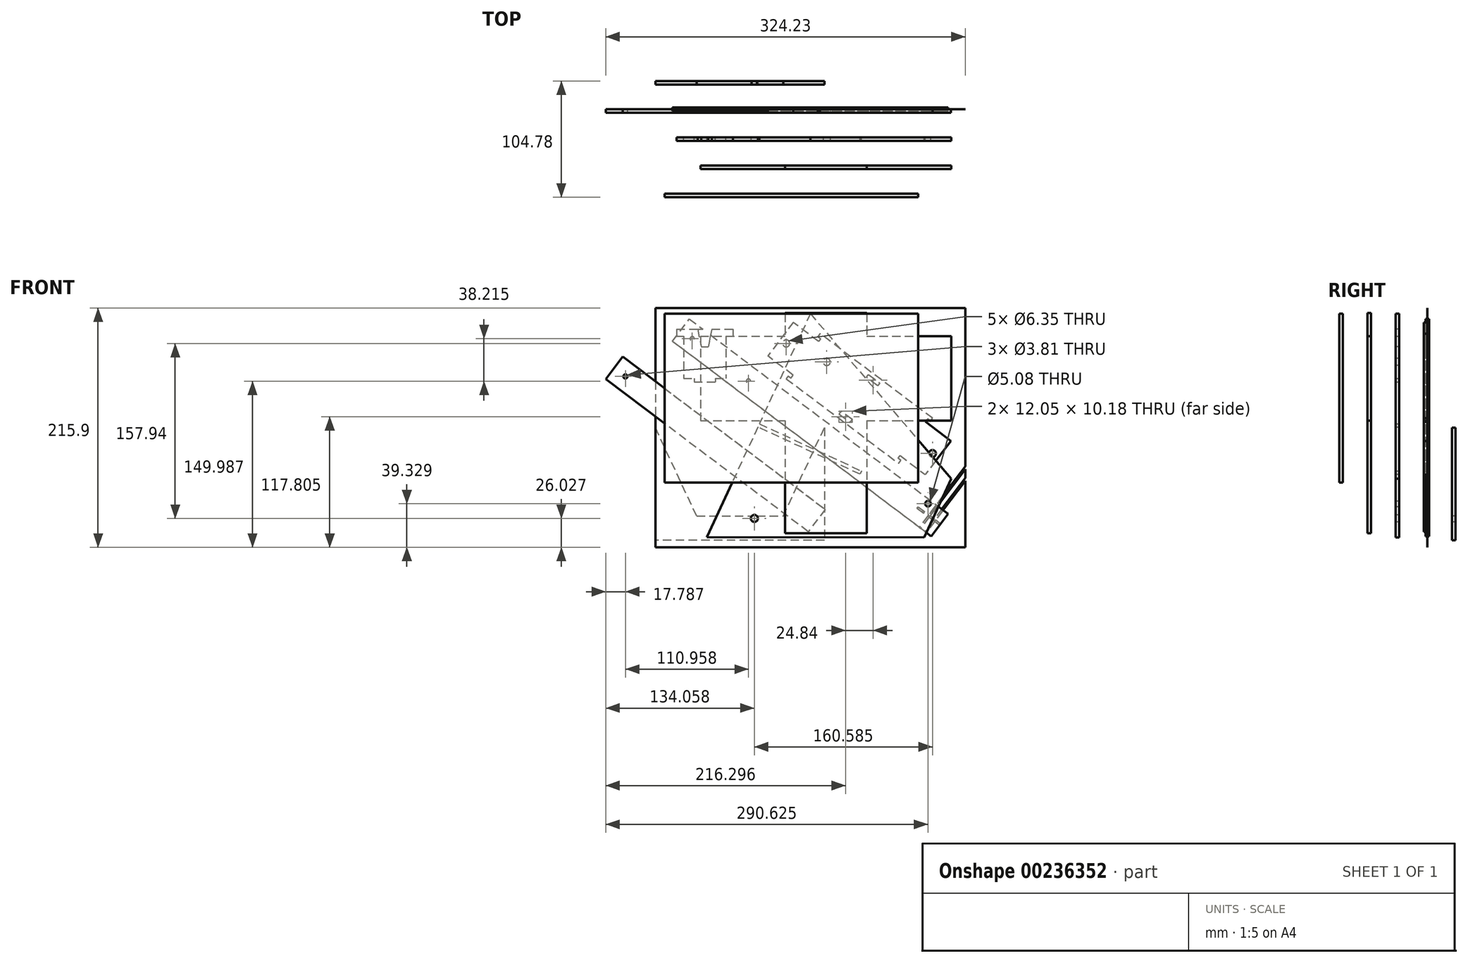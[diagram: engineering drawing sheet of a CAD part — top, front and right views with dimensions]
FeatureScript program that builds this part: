
annotation { "Feature Type Name" : "Feature", "Feature Type Description" : "" }
export const myFeature = defineFeature(function(context is Context, id is Id, definition is map)
    precondition{}
    {
        {
            var Q0;
            Q0=qCreatedBy(makeId("Front.planeOp"),FACE);
            var sketch = newSketch(context, id + "F0", { "sketchPlane" : qUnion([Q0])});
            skLineSegment(sketch, "E0.bottom", {"start": v(139.7, 107.95) * mm, "end": v(-139.7, 107.95) * mm});
            skLineSegment(sketch, "E0.top", {"start": v(139.7, -107.95) * mm, "end": v(-139.7, -107.95) * mm});
            skLineSegment(sketch, "E0.left", {"start": v(139.7, 107.95) * mm, "end": v(139.7, -107.95) * mm});
            skLineSegment(sketch, "E0.right", {"start": v(-139.7, 107.95) * mm, "end": v(-139.7, -107.95) * mm});
            skPoint(sketch, "E0.middle", {"position": v(0, 0) * mm});
            skSolve(sketch);
        }
        {
            var Q0;
            Q0=qCreatedBy(makeId("Front.planeOp"),FACE);
            var sketch = newSketch(context, id + "F1", { "sketchPlane" : qUnion([Q0])});
            skLineSegment(sketch, "E1.bottom", {"start": v(139.7, 107.95) * mm, "end": v(-139.7, 107.95) * mm, "construction": true});
            skLineSegment(sketch, "E1.top", {"start": v(139.7, -107.95) * mm, "end": v(-139.7, -107.95) * mm, "construction": true});
            skLineSegment(sketch, "E1.left", {"start": v(139.7, 107.95) * mm, "end": v(139.7, -107.95) * mm, "construction": true});
            skLineSegment(sketch, "E1.right", {"start": v(-139.7, 107.95) * mm, "end": v(-139.7, -107.95) * mm, "construction": true});
            skPoint(sketch, "E1.middle", {"position": v(0, 0) * mm});
            skLineSegment(sketch, "E2", {"start": v(-109, 98.04) * mm, "end": v(124.28, -77.75) * mm});
            skLineSegment(sketch, "E3", {"start": v(124.28, -77.75) * mm, "end": v(109, -98.04) * mm});
            skLineSegment(sketch, "E4", {"start": v(109, -98.04) * mm, "end": v(-124.28, 77.75) * mm});
            skLineSegment(sketch, "E5", {"start": v(-124.28, 77.75) * mm, "end": v(-109, 98.04) * mm});
            skLineSegment(sketch, "E6", {"start": v(-116.64, 87.9) * mm, "end": v(116.64, -87.9) * mm, "construction": true});
            skCircle(sketch, "E7", {"center": v(-55.78, 42.04) * mm, "radius": 1.9 * mm});
            skCircle(sketch, "E8", {"center": v(-106.5, 80.25) * mm, "radius": 1.9 * mm});
            skSolve(sketch);
        }
        {
            var Q0;
            Q0 = qSketchRegion(id + "F1", true);
            extrude(context, id + "F2", {"entities" : qUnion([Q0]), "endBound" : BoundingType.SYMMETRIC, "depth" : 3.17 * mm});
        }
        {
            var Q0;
            Q0=qCreatedBy(makeId("Front.planeOp"),FACE);
            cPlane(context, id + "F3", {"entities" : qUnion([Q0]), "cplaneType" : CPlaneType.OFFSET, "offset" : 25.4 * mm, "width" : 152.4 * mm, "height" : 152.4 * mm});
        }
        {
            var Q0;
            Q0=qCreatedBy(id+"F3.planeOp",FACE);
            var sketch = newSketch(context, id + "F4", { "sketchPlane" : qUnion([Q0])});
            skLineSegment(sketch, "E9", {"start": v(0, 102.87) * mm, "end": v(127, -46.1) * mm});
            skLineSegment(sketch, "E10", {"start": v(102.48, -99.13) * mm, "end": v(-93.28, -98.86) * mm});
            skLineSegment(sketch, "E11", {"start": v(0, 102.87) * mm, "end": v(-45.97, 3.45) * mm});
            skCircle(sketch, "E12", {"center": v(106.1, -68.62) * mm, "radius": 2.54 * mm});
            skLineSegment(sketch, "E13", {"start": v(-45.97, 3.45) * mm, "end": v(46.24, -39.2) * mm});
            skLineSegment(sketch, "E14", {"start": v(46.24, -39.2) * mm, "end": v(44.91, -42.08) * mm});
            skLineSegment(sketch, "E15", {"start": v(44.91, -42.08) * mm, "end": v(-47.3, 0.57) * mm});
            skLineSegment(sketch, "E16.trimOffspring", {"start": v(-47.3, 0.57) * mm, "end": v(-93.28, -98.86) * mm});
            skLineSegment(sketch, "E17", {"start": v(-45.97, 3.45) * mm, "end": v(-47.3, 0.57) * mm, "construction": true});
            skLineSegment(sketch, "E18", {"start": v(-46.64, 2) * mm, "end": v(45.58, -40.64) * mm, "construction": true});
            skLineSegment(sketch, "E19", {"start": v(127, -46.1) * mm, "end": v(102.48, -99.13) * mm});
            skLineSegment(sketch, "E20", {"start": v(114.74, -72.62) * mm, "end": v(106.1, -68.62) * mm, "construction": true});
            skSolve(sketch);
        }
        {
            var Q0;
            Q0 = qSketchRegion(id + "F4", true);
            extrude(context, id + "F5", {"entities" : qUnion([Q0]), "depth" : 3.17 * mm});
        }
        {
            var Q0;
            Q0=qCreatedBy(id+"F3.planeOp",FACE);
            var sketch = newSketch(context, id + "F6", { "sketchPlane" : qUnion([Q0])});
            skLineSegment(sketch, "E21.bottom", {"start": v(-120.65, 88.9) * mm, "end": v(-69.85, 88.9) * mm});
            skLineSegment(sketch, "E21.top", {"start": v(-120.65, 82.55) * mm, "end": v(-114.3, 82.55) * mm});
            skLineSegment(sketch, "E21.left", {"start": v(-120.65, 88.9) * mm, "end": v(-120.65, 82.55) * mm});
            skLineSegment(sketch, "E21.right", {"start": v(-69.85, 88.9) * mm, "end": v(-69.85, 82.55) * mm});
            skLineSegment(sketch, "E22.top", {"start": v(-114.3, 44.45) * mm, "end": v(-104.78, 44.45) * mm});
            skLineSegment(sketch, "E22.left", {"start": v(-114.3, 82.55) * mm, "end": v(-114.3, 44.45) * mm});
            skLineSegment(sketch, "E22.right", {"start": v(-76.2, 82.55) * mm, "end": v(-76.2, 44.45) * mm});
            skLineSegment(sketch, "E23.top", {"start": v(-104.78, 41.28) * mm, "end": v(-85.72, 41.28) * mm});
            skLineSegment(sketch, "E23.left", {"start": v(-85.73, 44.45) * mm, "end": v(-85.73, 41.28) * mm});
            skLineSegment(sketch, "E23.right", {"start": v(-104.78, 44.45) * mm, "end": v(-104.78, 41.28) * mm});
            skLineSegment(sketch, "E24", {"start": v(-95.25, 88.9) * mm, "end": v(-95.25, 41.28) * mm, "construction": true});
            skPoint(sketch, "E24.endSnap0", {"position": v(-95.25, 41.28) * mm});
            skLineSegment(sketch, "E25.trimOffspring", {"start": v(-76.2, 82.55) * mm, "end": v(-69.85, 82.55) * mm});
            skLineSegment(sketch, "E26.trimOffspring", {"start": v(-85.72, 44.45) * mm, "end": v(-76.2, 44.45) * mm});
            skSolve(sketch);
        }
        {
            var Q0;
            Q0 = qSketchRegion(id + "F6", true);
            extrude(context, id + "F7", {"entities" : qUnion([Q0]), "depth" : 3.17 * mm});
        }
        {
            var Q0;
            Q0=qCreatedBy(makeId("Front.planeOp"),FACE);
            var sketch = newSketch(context, id + "F8", { "sketchPlane" : qUnion([Q0])});
            skLineSegment(sketch, "E27", {"start": v(-21.81, 44.27) * mm, "end": v(79.61, -32.16) * mm});
            skLineSegment(sketch, "E28", {"start": v(79.61, -32.16) * mm, "end": v(81.52, -29.63) * mm});
            skLineSegment(sketch, "E29", {"start": v(110.19, 8.4) * mm, "end": v(8.76, 84.84) * mm});
            skLineSegment(sketch, "E30", {"start": v(8.76, 84.84) * mm, "end": v(6.85, 82.3) * mm});
            skLineSegment(sketch, "E31", {"start": v(13.69, 17.52) * mm, "end": v(44.26, 58.09) * mm, "construction": true});
            skLineSegment(sketch, "E32", {"start": v(74.69, 35.16) * mm, "end": v(44.11, -5.41) * mm, "construction": true});
            skLineSegment(sketch, "E33", {"start": v(-6.53, 64.55) * mm, "end": v(94.9, -11.88) * mm, "construction": true});
            skLineSegment(sketch, "E34", {"start": v(59.47, 46.62) * mm, "end": v(28.9, 6.05) * mm, "construction": true});
            skLineSegment(sketch, "E35", {"start": v(108.27, 5.87) * mm, "end": v(105.74, 7.78) * mm});
            skLineSegment(sketch, "E36", {"start": v(105.74, 7.78) * mm, "end": v(103.83, 5.25) * mm});
            skLineSegment(sketch, "E37", {"start": v(103.83, 5.25) * mm, "end": v(126.65, -11.95) * mm});
            skLineSegment(sketch, "E38.trimOffspring", {"start": v(108.27, 5.87) * mm, "end": v(110.19, 8.4) * mm});
            skLineSegment(sketch, "E39", {"start": v(52.49, 47.9) * mm, "end": v(62.63, 40.26) * mm});
            skLineSegment(sketch, "E40", {"start": v(62.63, 40.26) * mm, "end": v(60.72, 37.73) * mm});
            skLineSegment(sketch, "E41", {"start": v(60.72, 37.73) * mm, "end": v(50.58, 45.37) * mm});
            skLineSegment(sketch, "E42", {"start": v(50.58, 45.37) * mm, "end": v(52.49, 47.9) * mm});
            skLineSegment(sketch, "E43.MirrorCS", {"start": v(37.8, 7.3) * mm, "end": v(27.65, 14.94) * mm});
            skLineSegment(sketch, "E44.MirrorCS", {"start": v(25.74, 12.4) * mm, "end": v(35.88, 4.77) * mm});
            skLineSegment(sketch, "E45.MirrorCS", {"start": v(27.65, 14.94) * mm, "end": v(25.74, 12.4) * mm});
            skLineSegment(sketch, "E46.MirrorCS", {"start": v(35.88, 4.77) * mm, "end": v(37.8, 7.3) * mm});
            skLineSegment(sketch, "E47.MirrorCS", {"start": v(80.9, -25.18) * mm, "end": v(103.72, -42.38) * mm});
            skLineSegment(sketch, "E48.MirrorCS", {"start": v(78.99, -27.72) * mm, "end": v(80.9, -25.18) * mm});
            skLineSegment(sketch, "E49.MirrorCS", {"start": v(81.52, -29.63) * mm, "end": v(78.99, -27.72) * mm});
            skLineSegment(sketch, "E50.MirrorCS", {"start": v(7.47, 77.86) * mm, "end": v(-15.35, 95.05) * mm});
            skLineSegment(sketch, "E51.MirrorCS", {"start": v(9.38, 80.4) * mm, "end": v(7.47, 77.86) * mm});
            skLineSegment(sketch, "E52.MirrorCS", {"start": v(6.85, 82.3) * mm, "end": v(9.38, 80.4) * mm});
            skLineSegment(sketch, "E53.MirrorCS", {"start": v(-15.46, 47.43) * mm, "end": v(-38.28, 64.62) * mm});
            skLineSegment(sketch, "E54.MirrorCS", {"start": v(-17.37, 44.9) * mm, "end": v(-15.46, 47.43) * mm});
            skLineSegment(sketch, "E55.MirrorCS", {"start": v(-19.9, 46.8) * mm, "end": v(-17.37, 44.9) * mm});
            skLineSegment(sketch, "E56.trimOffspring", {"start": v(-19.9, 46.8) * mm, "end": v(-21.81, 44.27) * mm});
            skCircle(sketch, "E57", {"center": v(-21.74, 76.02) * mm, "radius": 3.18 * mm});
            skCircle(sketch, "E58.MirrorC", {"center": v(110.11, -23.34) * mm, "radius": 3.18 * mm});
            skLineSegment(sketch, "E59", {"start": v(-15.35, 95.05) * mm, "end": v(-15.35, 95.05) * mm});
            skLineSegment(sketch, "E60", {"start": v(-15.35, 95.05) * mm, "end": v(-38.28, 64.62) * mm});
            skLineSegment(sketch, "E61.MirrorCS", {"start": v(126.65, -11.95) * mm, "end": v(126.65, -11.95) * mm});
            skLineSegment(sketch, "E62.MirrorCS", {"start": v(126.65, -11.95) * mm, "end": v(103.72, -42.38) * mm});
            skSolve(sketch);
        }
        {
            var Q0;
            Q0 = qSketchRegion(id + "F8", true);
            extrude(context, id + "F9", {"entities" : qUnion([Q0]), "depth" : 3.17 * mm});
        }
        {
            var Q0;
            Q0=qCreatedBy(makeId("Front.planeOp"),FACE);
            cPlane(context, id + "F10", {"entities" : qUnion([Q0]), "cplaneType" : CPlaneType.OFFSET, "offset" : 25.4 * mm, "oppositeDirection" : true, "width" : 152.4 * mm, "height" : 152.4 * mm});
        }
        {
            var Q0;
            Q0=qCreatedBy(id+"F10.planeOp",FACE);
            var sketch = newSketch(context, id + "F11", { "sketchPlane" : qUnion([Q0])});
            skLineSegment(sketch, "E63.top", {"start": v(12.7, -101.6) * mm, "end": v(-139.7, -101.6) * mm});
            skLineSegment(sketch, "E63.left", {"start": v(12.7, 0) * mm, "end": v(12.7, -101.6) * mm});
            skLineSegment(sketch, "E63.right", {"start": v(-139.7, 0) * mm, "end": v(-139.7, -101.6) * mm});
            skPoint(sketch, "E63.middle", {"position": v(-63.5, -50.8) * mm});
            skLineSegment(sketch, "E64", {"start": v(-102.48, -79.82) * mm, "end": v(-24.52, -79.82) * mm});
            skLineSegment(sketch, "E65", {"start": v(-24.52, -79.82) * mm, "end": v(12.7, 0) * mm});
            skLineSegment(sketch, "E66", {"start": v(-102.48, -79.82) * mm, "end": v(-139.7, 0) * mm});
            skLineSegment(sketch, "E67", {"start": v(-63.5, 0) * mm, "end": v(-63.5, -101.6) * mm, "construction": true});
            skSolve(sketch);
        }
        {
            var Q0;
            Q0 = qSketchRegion(id + "F11", true);
            extrude(context, id + "F12", {"entities" : qUnion([Q0]), "depth" : 3.17 * mm});
        }
        {
            var Q0;
            Q0=qCreatedBy(makeId("Front.planeOp"),FACE);
            cPlane(context, id + "F13", {"entities" : qUnion([Q0]), "cplaneType" : CPlaneType.OFFSET, "offset" : 50.8 * mm, "width" : 152.4 * mm, "height" : 152.4 * mm});
        }
        {
            var Q0;
            Q0=qCreatedBy(id+"F13.planeOp",FACE);
            var sketch = newSketch(context, id + "F14", { "sketchPlane" : qUnion([Q0])});
            skLineSegment(sketch, "E68.bottom", {"start": v(-99.06, 82.55) * mm, "end": v(127, 82.55) * mm});
            skLineSegment(sketch, "E68.top", {"start": v(-99.06, 6.35) * mm, "end": v(127, 6.35) * mm});
            skLineSegment(sketch, "E68.left", {"start": v(-99.06, 82.55) * mm, "end": v(-99.06, 6.35) * mm});
            skLineSegment(sketch, "E68.right", {"start": v(127, 82.55) * mm, "end": v(127, 6.35) * mm});
            skLineSegment(sketch, "E69", {"start": v(13.97, 82.55) * mm, "end": v(13.97, 6.35) * mm, "construction": true});
            skLineSegment(sketch, "E70", {"start": v(-22.86, 82.55) * mm, "end": v(-22.86, 6.35) * mm, "construction": true});
            skLineSegment(sketch, "E71", {"start": v(50.8, 6.35) * mm, "end": v(50.8, 82.55) * mm, "construction": true});
            skSolve(sketch);
        }
        {
            var Q0;
            Q0 = qSketchRegion(id + "F14", true);
            extrude(context, id + "F15", {"entities" : qUnion([Q0]), "depth" : 3.17 * mm});
        }
        {
            var Q0;
            Q0=makeQuery(id+"F7.opExtrude","CAP_FACE",FACE,{"disambiguationData":[OSD([sQuery(id+"F6.wireOp",EDGE,"E21.bottom"),sQuery(id+"F6.wireOp",EDGE,"E21.top"),sQuery(id+"F6.wireOp",EDGE,"E21.left"),sQuery(id+"F6.wireOp",EDGE,"E21.right"),sQuery(id+"F6.wireOp",EDGE,"E22.top"),sQuery(id+"F6.wireOp",EDGE,"E22.left"),sQuery(id+"F6.wireOp",EDGE,"E22.right"),sQuery(id+"F6.wireOp",EDGE,"E23.top"),sQuery(id+"F6.wireOp",EDGE,"E23.left"),sQuery(id+"F6.wireOp",EDGE,"E23.right"),sQuery(id+"F6.wireOp",EDGE,"E25.trimOffspring"),sQuery(id+"F6.wireOp",EDGE,"E26.trimOffspring")])],"isStart":false});
            var sketch = newSketch(context, id + "F16", { "sketchPlane" : qUnion([Q0])});
            skLineSegment(sketch, "E72", {"start": v(-101.6, 88.9) * mm, "end": v(-98.42, 73.03) * mm});
            skLineSegment(sketch, "E73", {"start": v(-98.43, 73.03) * mm, "end": v(-95.25, 73.03) * mm});
            skLineSegment(sketch, "E74", {"start": v(-95.25, 73.03) * mm, "end": v(-95.25, 88.9) * mm, "construction": true});
            skLineSegment(sketch, "E75", {"start": v(-101.6, 88.9) * mm, "end": v(-95.25, 88.9) * mm});
            skLineSegment(sketch, "E76.MirrorCS", {"start": v(-92.08, 73.03) * mm, "end": v(-95.25, 73.03) * mm});
            skLineSegment(sketch, "E77.MirrorCS", {"start": v(-88.9, 88.9) * mm, "end": v(-92.08, 73.03) * mm});
            skLineSegment(sketch, "E78.MirrorCS", {"start": v(-88.9, 88.9) * mm, "end": v(-95.25, 88.9) * mm});
            skSolve(sketch);
        }
        {
            var Q0;
            Q0=makeQuery(id+"F16.imprint","IMPRINT",FACE,{"disambiguationData":[TD([[makeQuery(id+"F16.imprint","IMPRINT",EDGE,{"derivedFrom":sQuery(id+"F16.wireOp",EDGE,"E72")}),1.0]])]});
            extrude(context, id + "F17", {"entities" : qUnion([Q0]), "operationType" : NewBodyOperationType.REMOVE, "endBound" : BoundingType.THROUGH_ALL, "oppositeDirection" : true, "depth" : 25.4 * mm});
        }
        {
            var Q0;
            Q0=qCreatedBy(id+"F13.planeOp",FACE);
            cPlane(context, id + "F18", {"entities" : qUnion([Q0]), "cplaneType" : CPlaneType.OFFSET, "offset" : 25.4 * mm, "width" : 152.4 * mm, "height" : 152.4 * mm});
        }
        {
            var Q0;
            Q0=qCreatedBy(id+"F18.planeOp",FACE);
            var sketch = newSketch(context, id + "F19", { "sketchPlane" : qUnion([Q0])});
            skLineSegment(sketch, "E79.bottom", {"start": v(-131.52, 102.87) * mm, "end": v(97.08, 102.87) * mm});
            skLineSegment(sketch, "E79.top", {"start": v(-131.52, -49.53) * mm, "end": v(97.08, -49.53) * mm});
            skLineSegment(sketch, "E79.left", {"start": v(-131.52, 102.87) * mm, "end": v(-131.52, -49.53) * mm});
            skLineSegment(sketch, "E79.right", {"start": v(97.08, 102.87) * mm, "end": v(97.08, -49.53) * mm});
            skSolve(sketch);
        }
        {
            var Q0;
            Q0 = qSketchRegion(id + "F19", true);
            extrude(context, id + "F20", {"entities" : qUnion([Q0]), "depth" : 3.17 * mm});
        }
        {
            var Q0;
            Q0=makeQuery(id+"F15.opExtrude","CAP_FACE",FACE,{"disambiguationData":[OSD([sQuery(id+"F14.wireOp",EDGE,"E68.bottom"),sQuery(id+"F14.wireOp",EDGE,"E68.top"),sQuery(id+"F14.wireOp",EDGE,"E68.left"),sQuery(id+"F14.wireOp",EDGE,"E68.right")])],"isStart":false});
            var sketch = newSketch(context, id + "F21", { "sketchPlane" : qUnion([Q0])});
            skLineSegment(sketch, "E80.bottom", {"start": v(-22.86, 103.5) * mm, "end": v(50.8, 103.5) * mm});
            skLineSegment(sketch, "E80.top", {"start": v(-22.86, -95.25) * mm, "end": v(50.8, -95.25) * mm});
            skLineSegment(sketch, "E80.left", {"start": v(-22.86, 103.5) * mm, "end": v(-22.86, -95.25) * mm});
            skLineSegment(sketch, "E80.right", {"start": v(50.8, 103.5) * mm, "end": v(50.8, -95.25) * mm});
            skLineSegment(sketch, "E81", {"start": v(13.97, 103.5) * mm, "end": v(13.97, -95.25) * mm, "construction": true});
            skSolve(sketch);
        }
        {
            var Q0;
            Q0 = qSketchRegion(id + "F21", true);
            extrude(context, id + "F22", {"entities" : qUnion([Q0]), "operationType" : NewBodyOperationType.ADD, "oppositeDirection" : true, "depth" : 3.17 * mm});
        }
        {
            var Q0;
            Q0=makeQuery(id+"F5.opExtrude","CAP_FACE",FACE,{"disambiguationData":[OSD([sQuery(id+"F4.wireOp",EDGE,"E9"),sQuery(id+"F4.wireOp",EDGE,"E10"),sQuery(id+"F4.wireOp",EDGE,"E11"),sQuery(id+"F4.wireOp",EDGE,"E12"),sQuery(id+"F4.wireOp",EDGE,"E13"),sQuery(id+"F4.wireOp",EDGE,"E14"),sQuery(id+"F4.wireOp",EDGE,"E15"),sQuery(id+"F4.wireOp",EDGE,"E16.trimOffspring"),sQuery(id+"F4.wireOp",EDGE,"E19")])],"isStart":false});
            var sketch = newSketch(context, id + "F23", { "sketchPlane" : qUnion([Q0])});
            skCircle(sketch, "E82", {"center": v(-50.47, -81.92) * mm, "radius": 3.18 * mm});
            skCircle(sketch, "E83", {"center": v(14.83, 59.29) * mm, "radius": 3.18 * mm});
            skSolve(sketch);
        }
        {
            var Q0;
            Q0 = qSketchRegion(id + "F23", true);
            extrude(context, id + "F24", {"entities" : qUnion([Q0]), "operationType" : NewBodyOperationType.REMOVE, "endBound" : BoundingType.THROUGH_ALL, "oppositeDirection" : true, "depth" : 25.4 * mm});
        }
        {
            var Q0;
            Q0=makeQuery(id+"F0.imprint","IMPRINT",FACE,{"disambiguationData":[TD([[makeQuery(id+"F0.imprint","IMPRINT",EDGE,{"derivedFrom":sQuery(id+"F0.wireOp",EDGE,"E0.bottom")}),1.0]])]});
            extrude(context, id + "F25", {"entities" : qUnion([Q0]), "depth" : 0.03 * mm});
        }
        {
            var Q0;
            Q0=makeQuery(id+"F25.opExtrude","CAP_FACE",FACE,{"disambiguationData":[OSD([sQuery(id+"F0.wireOp",EDGE,"E0.bottom"),sQuery(id+"F0.wireOp",EDGE,"E0.top"),sQuery(id+"F0.wireOp",EDGE,"E0.left"),sQuery(id+"F0.wireOp",EDGE,"E0.right")])],"isStart":false});
            var sketch = newSketch(context, id + "F26", { "sketchPlane" : qUnion([Q0])});
            skLineSegment(sketch, "E84.bottom", {"start": v(54.1, 93.02) * mm, "end": v(-225.3, 93.02) * mm, "construction": true});
            skLineSegment(sketch, "E84.top", {"start": v(54.1, -122.88) * mm, "end": v(-225.3, -122.88) * mm, "construction": true});
            skLineSegment(sketch, "E84.left", {"start": v(54.1, 93.02) * mm, "end": v(54.1, -122.88) * mm, "construction": true});
            skLineSegment(sketch, "E84.right", {"start": v(-225.3, 93.02) * mm, "end": v(-225.3, -122.88) * mm, "construction": true});
            skPoint(sketch, "E84.middle", {"position": v(-85.6, -14.93) * mm});
            skLineSegment(sketch, "E85", {"start": v(-169.24, 64) * mm, "end": v(13.33, -73.58) * mm});
            skLineSegment(sketch, "E86", {"start": v(13.33, -73.58) * mm, "end": v(-1.96, -93.86) * mm});
            skLineSegment(sketch, "E87", {"start": v(-1.96, -93.86) * mm, "end": v(-184.53, 43.71) * mm});
            skLineSegment(sketch, "E88", {"start": v(-184.53, 43.71) * mm, "end": v(-169.24, 64) * mm});
            skLineSegment(sketch, "E89", {"start": v(-176.89, 53.86) * mm, "end": v(5.68, -83.72) * mm, "construction": true});
            skCircle(sketch, "E90", {"center": v(-166.74, 46.21) * mm, "radius": 1.9 * mm});
            skSolve(sketch);
        }
        {
            var Q0;
            Q0 = qSketchRegion(id + "F26", true);
            extrude(context, id + "F27", {"entities" : qUnion([Q0]), "depth" : 3.17 * mm});
        }
        {
            var Q0;
            Q0=makeQuery(id+"F2.opExtrude","SWEPT_FACE",FACE,{"disambiguationData":[OSD([sQuery(id+"F1.wireOp",EDGE,"E3")])]});
            var sketch = newSketch(context, id + "F28", { "sketchPlane" : qUnion([Q0])});
            skCircle(sketch, "E91", {"center": v(0, 0.76) * mm, "radius": 0.76 * mm});
            skSolve(sketch);
        }
        {
            var Q0;
            Q0 = qSketchRegion(id + "F28", true);
            extrude(context, id + "F29", {"entities" : qUnion([Q0]), "operationType" : NewBodyOperationType.REMOVE, "oppositeDirection" : true, "depth" : 25.4 * mm});
        }
        {
            var Q0;
            Q0=makeQuery(id+"F2.opExtrude","SWEPT_FACE",FACE,{"disambiguationData":[OSD([sQuery(id+"F1.wireOp",EDGE,"E4")])]});
            var sketch = newSketch(context, id + "F30", { "sketchPlane" : qUnion([Q0])});
            skCircle(sketch, "E92", {"center": v(139.7, 0) * mm, "radius": 0.76 * mm});
            skCircle(sketch, "E93", {"center": v(133.35, 0) * mm, "radius": 0.76 * mm});
            skSolve(sketch);
        }
        {
            var Q0;
            Q0 = qSketchRegion(id + "F30", true);
            extrude(context, id + "F31", {"entities" : qUnion([Q0]), "operationType" : NewBodyOperationType.REMOVE, "endBound" : BoundingType.THROUGH_ALL, "oppositeDirection" : true, "depth" : 25.4 * mm});
        }
    });
